# Revit family: Electronics_Visual-TVs_ViewSonic_ViewSonicR-EP1042T-Digital-ePoster-Display
name_source: partatom
category: Electrical Equipment
revit_build: Autodesk Revit 2017 (Build: 20190508_0315(x64)
units: mm (PartAtom-declared; Revit-internal decimal feet)

## family parameters
Always vertical = Yes
Cut with Voids When Loaded = No
OmniClass Number = 23.85.10.14.24.17
OmniClass Title = Plasma Video Monitors
Panel Configuration = Two Columns, Circuits Across
Part Type = Panelboard
Room Calculation Point = No
Round Connector Dimension = Use Diameter
Shared = No
Work Plane-Based = No

## types (1)
- EP 1042 T
    Aspect Ratio = 16:10
    Assembly Code = D5030500
    Backlight = WLED
    Backlight Life = 10,000 Hours (typ.)
    Brightness = 300 nits (typ.)
    Colors = 262K Color
    Contrast Ratio = 800:1 (typ.)
    Cover Material = Plastic - ViewSonic - Black
    Covering Color = Plastic - ViewSonic - Black
    Description = The ViewSonic EP1042T is a 10" (10.1" viewable) all-in-one interactive digital ePoster designed as a conference and meeting arrangement solution, delivering eye-catching and touch-interactive commercial messaging. Adopting the latest power-over-Ethernet (POE) technology, the display can be easily installed at high-visibility locations via one LAN cable. The EP1042T features a wireless b/g/n network and LAN connectivity for easy content loading. Multi-touch compatibility with HTML5 and SMIL formats deliver a 2-way interactive platform for dynamic, customized content. Its built-in media player, 8GB internal storage, and integrated speakers enable the playback of video clips, as well as photos and music, from a USB hard drive or SD/SDHC memory card. Bundled with Signage Manager Express software, the EP1042T effectively delivers customized messaging to target audiences. With VESA-mount compliance (75mm x 75mm), the EP1042T is installation-ready for high-visibility, high-traffic locations.
    Display Area (mm) = 216.96(W) x 135.6(H)
    Display Size = 10"
    Edition number = 1
    Keynote = 11130
    Light Source = LED
    Manufacturer = ViewSonic
    Model = viewsonic_ep1042t
    Orientation = Landscape
    Panel Size = 10" (10.1'' diagonal)
    Product Guid = 2cad4a07-35e2-4920-a62a-07bfac7ef922
    Product data url = https://www.bimobject.com
    Resolution = 1280 x 800; 16:9
    Response Time = 25 ms
    Screen Material = Screen - ViewSonic - EP1042
    Type/ Tech = TFT LCD Module with LED Backlight
    URL = https://www.viewsonic.com
    Viewable Area (In.) = 10"
    Viewing Angles = Top = 85, Bottom = 85, Left = 85, Right = 85 (typ.)

## geometry (parser evidence)
native form markers: Sweep x4
no freeform markers — native parametric forms only
